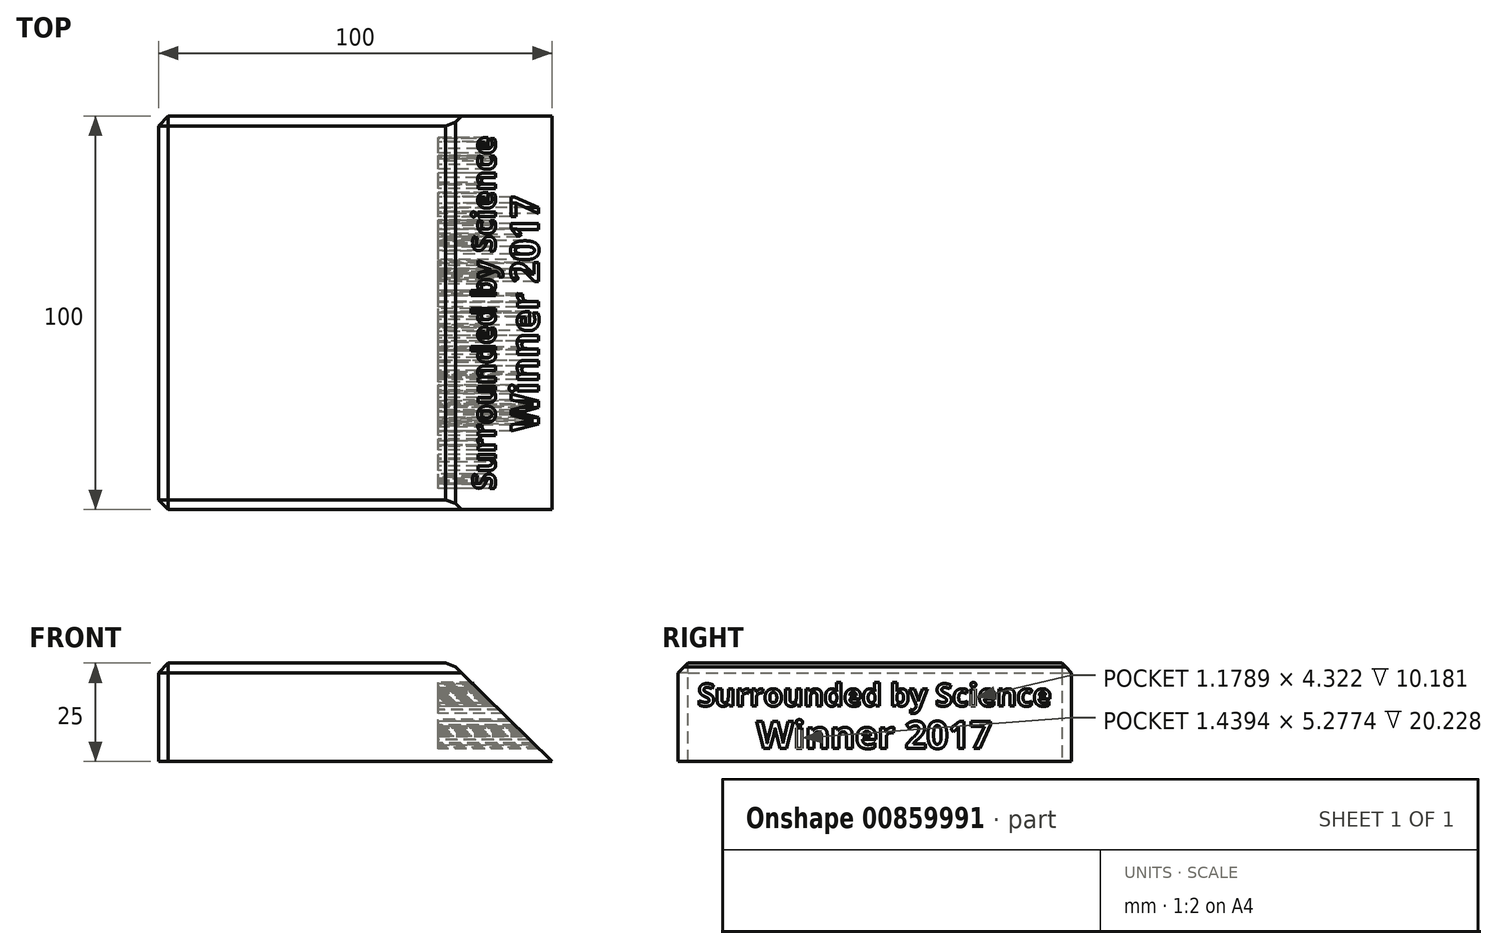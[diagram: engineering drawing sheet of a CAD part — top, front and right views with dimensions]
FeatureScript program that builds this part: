
annotation { "Feature Type Name" : "Feature", "Feature Type Description" : "" }
export const myFeature = defineFeature(function(context is Context, id is Id, definition is map)
    precondition{}
    {
        {
            var Q0;
            Q0=qCreatedBy(makeId("Front.planeOp"),FACE);
            var sketch = newSketch(context, id + "F0", { "sketchPlane" : qUnion([Q0])});
            skLineSegment(sketch, "E0.bottom", {"start": v(50, 12.5) * mm, "end": v(-50, 12.5) * mm});
            skLineSegment(sketch, "E0.top", {"start": v(50, -12.5) * mm, "end": v(-50, -12.5) * mm});
            skLineSegment(sketch, "E0.left", {"start": v(50, 12.5) * mm, "end": v(50, -12.5) * mm});
            skLineSegment(sketch, "E0.right", {"start": v(-50, 12.5) * mm, "end": v(-50, -12.5) * mm});
            skPoint(sketch, "E0.middle", {"position": v(0, 0) * mm});
            skLineSegment(sketch, "E1", {"start": v(50, -12.5) * mm, "end": v(24.43, 12.5) * mm});
            skSolve(sketch);
        }
        {
            var Q0;
            Q0=makeQuery(id+"F0.imprint","IMPRINT",FACE,{"disambiguationData":[TD([[makeQuery(id+"F0.imprint","IMPRINT",EDGE,{"derivedFrom":sQuery(id+"F0.wireOp",EDGE,"E0.top")}),-1.0]])]});
            extrude(context, id + "F1", {"entities" : qUnion([Q0]), "depth" : 100 * mm, "offsetDistance" : 25 * mm});
        }
        {
            var Q0;
            Q0=qCreatedBy(makeId("Right.planeOp"),FACE);
            var sketch = newSketch(context, id + "F2", { "sketchPlane" : qUnion([Q0])});
            skText(sketch, "E2", { "text": "Surrounded by Science", "fontName": "OpenSans-Bold.ttf"});
            skText(sketch, "E3", { "text": "Winner 2017", "fontName": "OpenSans-Bold.ttf"});
            const initialGuessF2  = {"E2": [-0.095, 0.00158, 1, 0, 0.0057], "E3": [-0.08, -0.0092, 1, 0, 0.00696]};
            skSetInitialGuess(sketch, initialGuessF2);
            skSolve(sketch);
        }
        {
            var Q0;
            Q0 = qSketchRegion(id + "F2", true);
            extrude(context, id + "F3", {"entities" : qUnion([Q0]), "operationType" : NewBodyOperationType.REMOVE, "depth" : 47.3 * mm, "offsetDistance" : 25 * mm});
        }
        {
            var Q0;
            Q0=makeQuery(id+"F1.opExtrude","CAP_EDGE",EDGE,{"disambiguationData":[OSD([sQuery(id+"F0.wireOp",EDGE,"E0.bottom")])],"isStart":false});
            var Q1;
            Q1=makeQuery(id+"F1.opExtrude","SWEPT_EDGE",EDGE,{"disambiguationData":[OSD([sQuery(id+"F0.wireOp",EDGE,"E0.bottom"),sQuery(id+"F0.wireOp",EDGE,"E0.right")])]});
            var Q2;
            Q2=makeQuery(id+"F1.opExtrude","CAP_EDGE",EDGE,{"disambiguationData":[OSD([sQuery(id+"F0.wireOp",EDGE,"E0.bottom")])],"isStart":true});
            var Q3;
            Q3=makeQuery(id+"F1.opExtrude","CAP_EDGE",EDGE,{"disambiguationData":[OSD([sQuery(id+"F0.wireOp",EDGE,"E0.right")])],"isStart":true});
            var Q4;
            Q4=makeQuery(id+"F1.opExtrude","CAP_EDGE",EDGE,{"disambiguationData":[OSD([sQuery(id+"F0.wireOp",EDGE,"E0.right")])],"isStart":false});
            chamfer(context, id + "F4", {"entities" : qUnion([Q0, Q1, Q2, Q3, Q4]), "width" : 2.5 * mm, "tangentPropagation" : true});
        }
        {
            var Q0;
            Q0=makeQuery(id+"F1.opExtrude","SWEPT_EDGE",EDGE,{"disambiguationData":[OSD([sQuery(id+"F0.wireOp",EDGE,"E0.bottom"),sQuery(id+"F0.wireOp",EDGE,"E1")])]});
            chamfer(context, id + "F5", {"entities" : qUnion([Q0]), "width" : 3.5 * mm, "tangentPropagation" : true});
        }
        {
            var Q0;
            Q0 = qSketchRegion(id + "F2", true);
            extrude(context, id + "F6", {"entities" : qUnion([Q0]), "operationType" : NewBodyOperationType.ADD, "depth" : 21 * mm, "offsetDistance" : 25 * mm});
        }
    });
